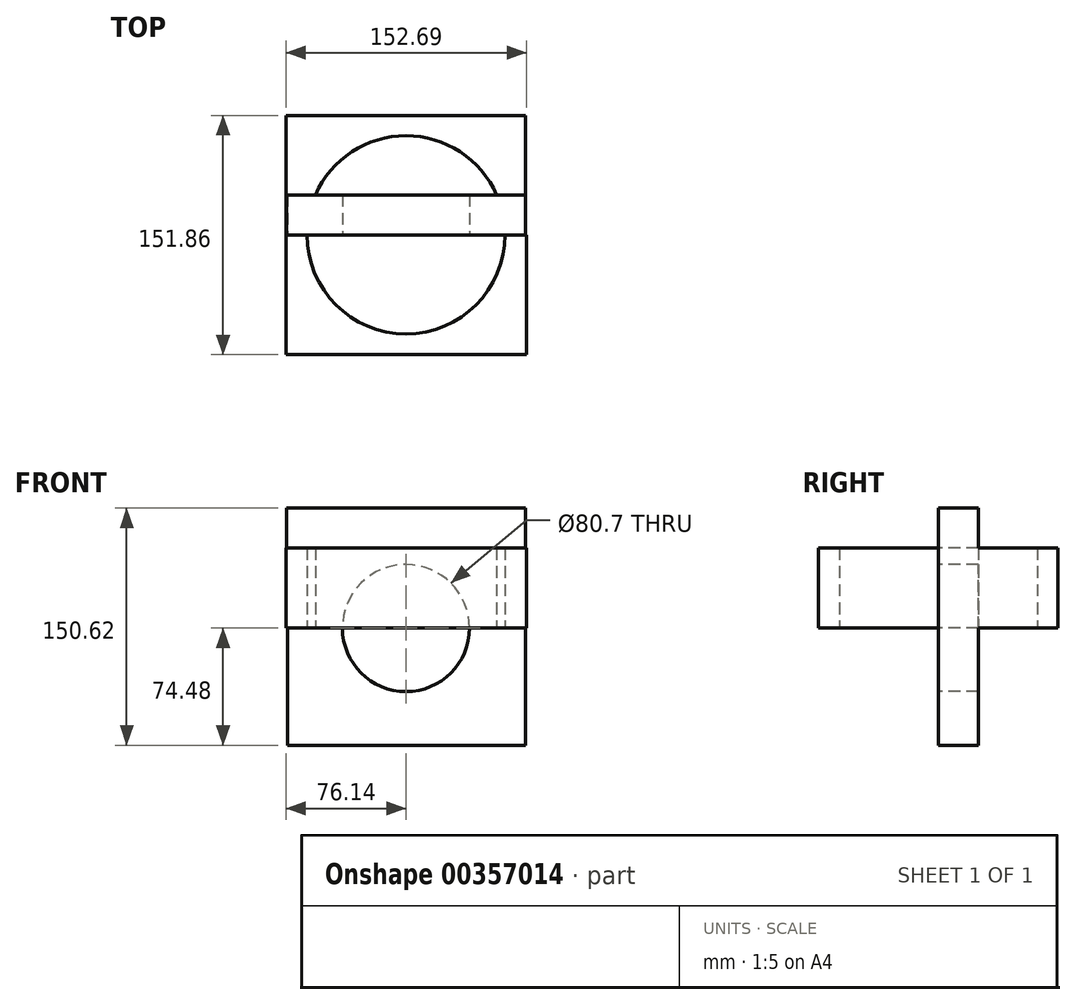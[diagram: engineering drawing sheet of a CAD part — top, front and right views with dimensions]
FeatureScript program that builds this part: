
annotation { "Feature Type Name" : "Feature", "Feature Type Description" : "" }
export const myFeature = defineFeature(function(context is Context, id is Id, definition is map)
    precondition{}
    {
        {
            var Q0;
            Q0=qCreatedBy(makeId("Front.planeOp"),FACE);
            var sketch = newSketch(context, id + "F0", { "sketchPlane" : qUnion([Q0])});
            skCircle(sketch, "E0", {"center": v(0, 0) * mm, "radius": 40.35 * mm});
            skLineSegment(sketch, "E1.bottom", {"start": v(-75.93, 0) * mm, "end": v(75.93, 0) * mm});
            skLineSegment(sketch, "E1.top", {"start": v(-75.93, 76.14) * mm, "end": v(75.93, 76.14) * mm});
            skLineSegment(sketch, "E1.left", {"start": v(-75.93, 0) * mm, "end": v(-75.93, 76.14) * mm});
            skLineSegment(sketch, "E1.right", {"start": v(75.93, 0) * mm, "end": v(75.93, 76.14) * mm});
            skLineSegment(sketch, "E2.bottom", {"start": v(-75.3, -74.48) * mm, "end": v(75.93, -74.48) * mm});
            skLineSegment(sketch, "E2.top", {"start": v(-75.3, 0) * mm, "end": v(75.93, 0) * mm});
            skLineSegment(sketch, "E2.left", {"start": v(-75.3, -74.48) * mm, "end": v(-75.3, 0) * mm});
            skLineSegment(sketch, "E2.right", {"start": v(75.93, -74.48) * mm, "end": v(75.93, 0) * mm});
            skSolve(sketch);
        }
        {
            var Q0;
            Q0 = qSketchRegion(id + "F0", true);
            extrude(context, id + "F1", {"entities" : qUnion([Q0]), "oppositeDirection" : true, "depth" : 25.4 * mm});
        }
        {
            var Q0;
            Q0=qCreatedBy(makeId("Top.planeOp"),FACE);
            var sketch = newSketch(context, id + "F2", { "sketchPlane" : qUnion([Q0])});
            skCircle(sketch, "E3", {"center": v(0, 0) * mm, "radius": 62.9 * mm});
            skLineSegment(sketch, "E4.bottom", {"start": v(-76.14, 0) * mm, "end": v(76.55, 0) * mm});
            skLineSegment(sketch, "E4.top", {"start": v(-76.14, -76.14) * mm, "end": v(76.55, -76.14) * mm});
            skLineSegment(sketch, "E4.left", {"start": v(-76.14, 0) * mm, "end": v(-76.14, -76.14) * mm});
            skLineSegment(sketch, "E4.right", {"start": v(76.55, 0) * mm, "end": v(76.55, -76.14) * mm});
            skLineSegment(sketch, "E5.bottom", {"start": v(-76.14, 0) * mm, "end": v(75.93, 0) * mm});
            skLineSegment(sketch, "E5.top", {"start": v(-76.14, 75.72) * mm, "end": v(75.93, 75.72) * mm});
            skLineSegment(sketch, "E5.left", {"start": v(-76.14, 0) * mm, "end": v(-76.14, 75.72) * mm});
            skLineSegment(sketch, "E5.right", {"start": v(75.93, 0) * mm, "end": v(75.93, 75.72) * mm});
            skSolve(sketch);
        }
        {
            var Q0;
            Q0 = qSketchRegion(id + "F2", true);
            extrude(context, id + "F3", {"entities" : qUnion([Q0]), "operationType" : NewBodyOperationType.ADD, "depth" : 50.8 * mm});
        }
    });
